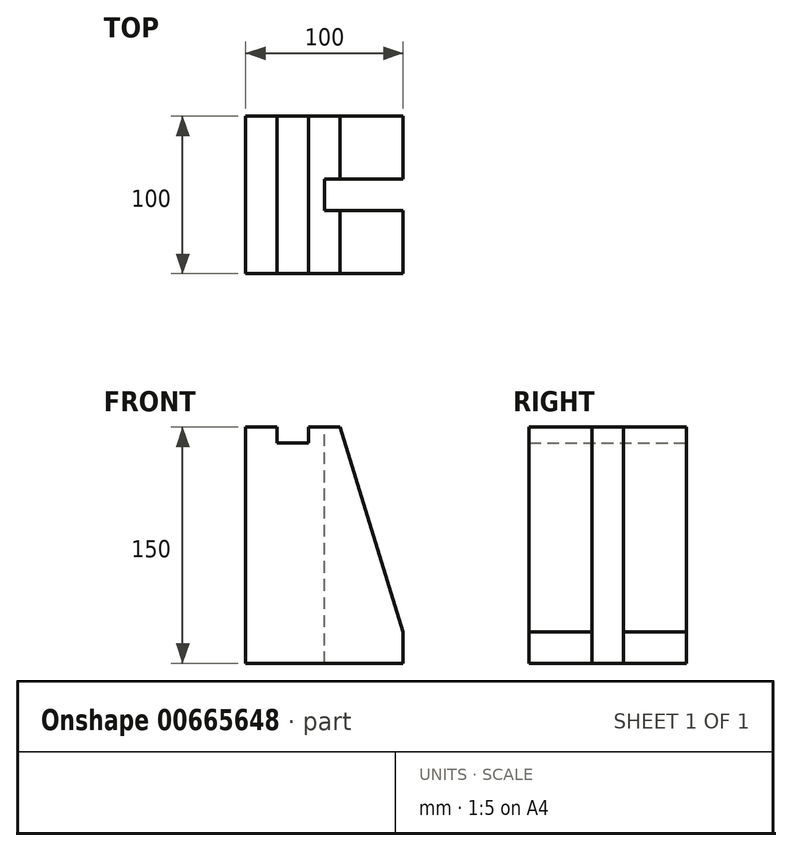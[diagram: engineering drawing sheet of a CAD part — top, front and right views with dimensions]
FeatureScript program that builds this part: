
annotation { "Feature Type Name" : "Feature", "Feature Type Description" : "" }
export const myFeature = defineFeature(function(context is Context, id is Id, definition is map)
    precondition{}
    {
        {
            var Q0;
            Q0=qCreatedBy(makeId("Front.planeOp"),FACE);
            var sketch = newSketch(context, id + "F0", { "sketchPlane" : qUnion([Q0])});
            skLineSegment(sketch, "E0", {"start": v(0, 0) * mm, "end": v(100, 0) * mm});
            skLineSegment(sketch, "E1", {"start": v(100, 0) * mm, "end": v(100, 20) * mm});
            skLineSegment(sketch, "E2", {"start": v(0, 0) * mm, "end": v(0, 150) * mm});
            skLineSegment(sketch, "E3", {"start": v(0, 150) * mm, "end": v(20, 150) * mm});
            skLineSegment(sketch, "E4", {"start": v(20, 150) * mm, "end": v(20, 140) * mm});
            skLineSegment(sketch, "E5", {"start": v(20, 140) * mm, "end": v(40, 140) * mm});
            skLineSegment(sketch, "E6", {"start": v(40, 140) * mm, "end": v(40, 150) * mm});
            skLineSegment(sketch, "E7", {"start": v(40, 150) * mm, "end": v(60, 150) * mm});
            skLineSegment(sketch, "E8", {"start": v(60, 150) * mm, "end": v(100, 20) * mm});
            skSolve(sketch);
        }
        {
            var Q0;
            Q0=makeQuery(id+"F0.imprint","IMPRINT",FACE,{"disambiguationData":[TD([[makeQuery(id+"F0.imprint","IMPRINT",EDGE,{"derivedFrom":sQuery(id+"F0.wireOp",EDGE,"E0")}),1.0]])]});
            extrude(context, id + "F1", {"entities" : qUnion([Q0]), "depth" : 100 * mm, "offsetDistance" : 25 * mm});
        }
        {
            var Q0;
            {var subQ0=sQuery(id+"FUlaHXm4ibbxiFo_1.wireOp",EDGE,"VbDxquym-kzYz-iZ4z-ARLs-QYovFN7K0P4P");Q0=makeQuery(id+"FUlaHXm4ibbxiFo_1.imprint","IMPRINT",FACE,{"disambiguationData":[TD([[makeQuery(id+"FUlaHXm4ibbxiFo_1.imprint","IMPRINT",EDGE,{"derivedFrom":subQ0}),1.0]])]});}
            var sketch = newSketch(context, id + "F2", { "sketchPlane" : qUnion([Q0])});
            skLineSegment(sketch, "E9", {"start": v(48.48, -59.88) * mm, "end": v(48.48, -39.88) * mm});
            skSolve(sketch);
        }
        {
            var Q0;
            Q0=makeQuery(id+"F1.opExtrude","SWEPT_FACE",FACE,{"disambiguationData":[OSD([sQuery(id+"F0.wireOp",EDGE,"E7")])]});
            var sketch = newSketch(context, id + "F3", { "sketchPlane" : qUnion([Q0])});
            skLineSegment(sketch, "E10", {"start": v(60, -50) * mm, "end": v(60, -60) * mm});
            skLineSegment(sketch, "E11", {"start": v(60, -60) * mm, "end": v(50, -60) * mm});
            skLineSegment(sketch, "E12", {"start": v(50, -60) * mm, "end": v(50, -40) * mm});
            skLineSegment(sketch, "E13", {"start": v(60, -50) * mm, "end": v(60, -40) * mm});
            skLineSegment(sketch, "E14", {"start": v(60, -40) * mm, "end": v(50, -40) * mm});
            skSolve(sketch);
        }
        {
            var Q0;
            Q0=makeQuery(id+"F3.imprint","IMPRINT",FACE,{"disambiguationData":[TD([[makeQuery(id+"F3.imprint","IMPRINT",EDGE,{"derivedFrom":sQuery(id+"F3.wireOp",EDGE,"E10")}),1.0]])]});
            extrude(context, id + "F4", {"entities" : qUnion([Q0]), "operationType" : NewBodyOperationType.REMOVE, "oppositeDirection" : true, "depth" : 150 * mm, "offsetDistance" : 25 * mm});
        }
        {
            var Q0;
            Q0=makeQuery(id+"F4.boolean.opBoolean","COPY",FACE,{"derivedFrom":makeQuery(id+"F4.opExtrude","SWEPT_FACE",FACE,{"disambiguationData":[OSD([sQuery(id+"F3.wireOp",EDGE,"E10"),sQuery(id+"F3.wireOp",EDGE,"E13")])]})});
            extrude(context, id + "F5", {"entities" : qUnion([Q0]), "operationType" : NewBodyOperationType.REMOVE, "oppositeDirection" : true, "depth" : 100 * mm, "offsetDistance" : 25 * mm});
        }
    });
